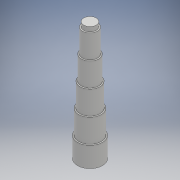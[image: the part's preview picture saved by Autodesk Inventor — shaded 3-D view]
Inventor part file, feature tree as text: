
AUTODESK INVENTOR PART (.ipt)
format: ipt  version: 2018 (Build 220112000, 112)  size: 138,752 bytes
history: native  units: mm
features: extrude x9, sketch x9
ambient origin geometry x8: Origin, YZ Plane, XZ Plane, XY Plane, X Axis, Y Axis, Z Axis, Center Point
bodies: Solid1 (feature_tree)
feature tree (18):
  extrude  "Extrusion1"  Depth=3.0mm TaperAngle=0.0deg
  extrude  "Extrusion2"  Depth=18.18mm TaperAngle=0.0deg
  extrude  "Extrusion3"  Depth=18.8mm TaperAngle=0.0deg
  extrude  "Extrusion4"  Depth=18.8mm TaperAngle=0.0deg
  extrude  "Extrusion5"  Depth=18.8mm TaperAngle=0.0deg
  extrude  "Extrusion6"  Depth=18.8mm TaperAngle=0.0deg
  extrude  "Extrusion7"  Depth=3.62mm TaperAngle=0.0deg
  extrude  "Extrusion8"  Depth=5.0mm TaperAngle=0.0deg
  extrude  "Extrusion9"  Depth=30.0mm TaperAngle=0.0deg
  sketch  "Sketch1"  dims[d0=30.0mm d1=3.0mm d2=0.0mm]
  sketch  "Sketch2"  dims[d3=20.0mm d4=18.18mm d5=0.0mm]
  sketch  "Sketch3"  dims[d6=18.0mm d7=18.8mm d8=0.0mm]
  sketch  "Sketch4"  dims[d9=16.0mm d10=18.8mm d11=0.0mm]
  sketch  "Sketch5"  dims[d12=14.0mm d13=18.8mm d14=0.0mm]
  sketch  "Sketch6"  dims[d15=12.0mm d16=18.8mm d17=0.0mm]
  sketch  "Sketch7"  dims[d18=10.0mm d19=3.62mm d20=0.0mm]
  sketch  "Sketch8"  dims[d21=40.0mm d22=5.0mm d23=0.0mm]
  sketch  "Sketch9"  dims[d24=3.5mm d25=30.0mm d26=0.0mm]
